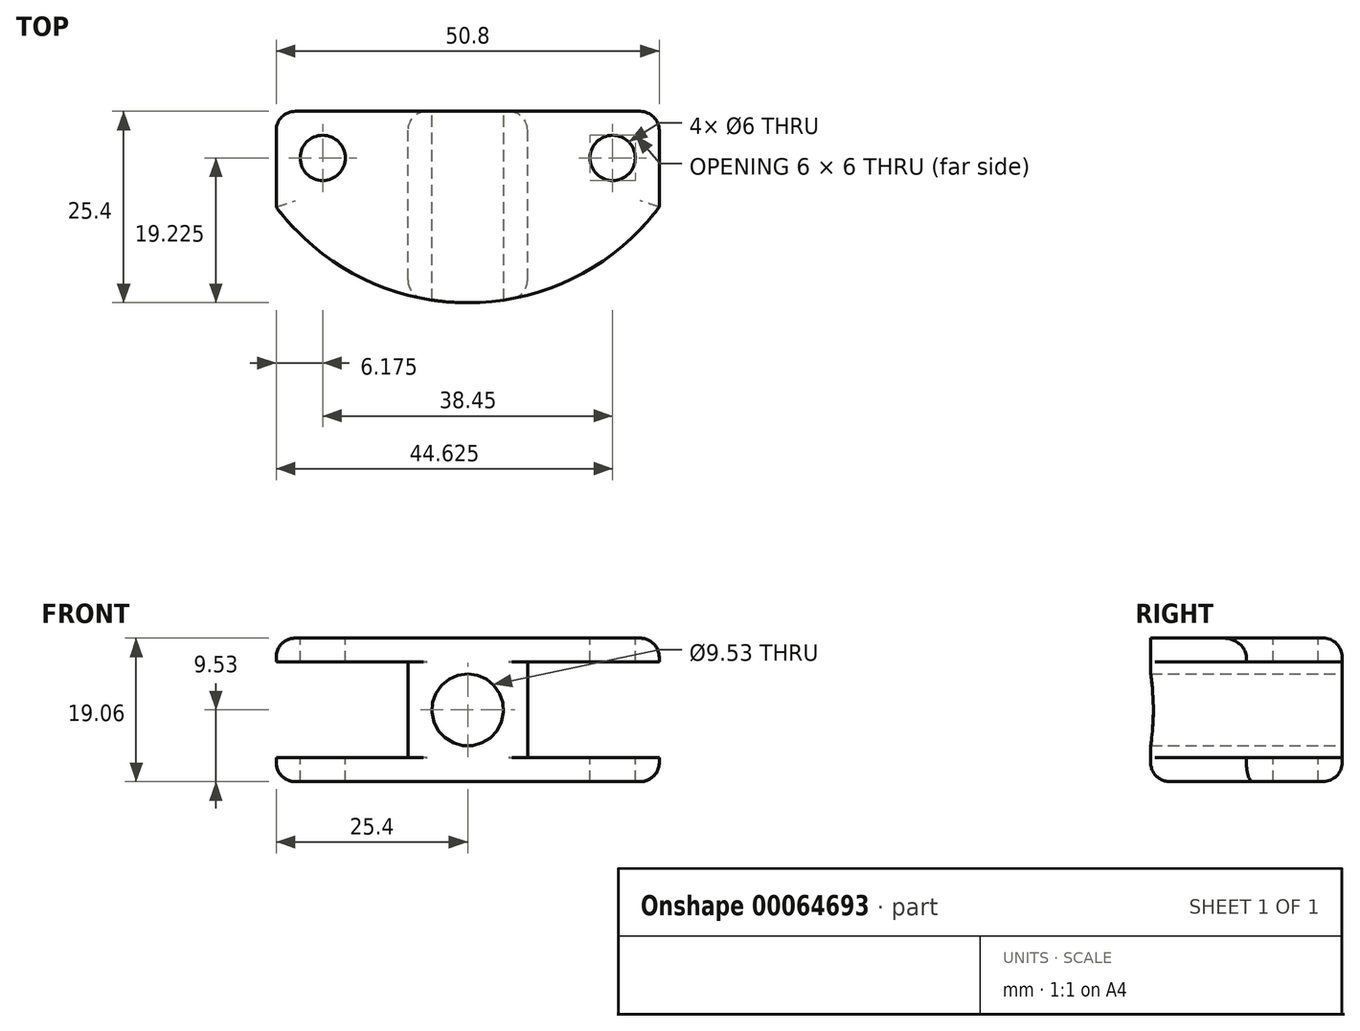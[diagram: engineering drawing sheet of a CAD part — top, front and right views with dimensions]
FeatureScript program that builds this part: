
annotation { "Feature Type Name" : "Feature", "Feature Type Description" : "" }
export const myFeature = defineFeature(function(context is Context, id is Id, definition is map)
    precondition{}
    {
        {
            var Q0;
            Q0=qCreatedBy(makeId("Front.planeOp"),FACE);
            var sketch = newSketch(context, id + "F0", { "sketchPlane" : qUnion([Q0])});
            skLineSegment(sketch, "E0", {"start": v(0, 19.05) * mm, "end": v(-38.1, 19.05) * mm});
            skLineSegment(sketch, "E1", {"start": v(-38.1, 19.05) * mm, "end": v(-38.1, 12.7) * mm});
            skLineSegment(sketch, "E2", {"start": v(0, -19.05) * mm, "end": v(-38.1, -19.05) * mm});
            skLineSegment(sketch, "E3", {"start": v(-38.1, -19.05) * mm, "end": v(-38.1, -12.7) * mm});
            skLineSegment(sketch, "E4", {"start": v(-38.1, 12.7) * mm, "end": v(-15.88, 12.7) * mm});
            skLineSegment(sketch, "E5", {"start": v(-15.88, 12.7) * mm, "end": v(-15.88, -12.7) * mm});
            skLineSegment(sketch, "E6", {"start": v(-15.88, -12.7) * mm, "end": v(-38.1, -12.7) * mm});
            skLineSegment(sketch, "E7.MirrorCS", {"start": v(0, 19.05) * mm, "end": v(38.1, 19.05) * mm});
            skLineSegment(sketch, "E8.MirrorCS", {"start": v(38.1, 19.05) * mm, "end": v(38.1, 12.7) * mm});
            skLineSegment(sketch, "E9.MirrorCS", {"start": v(38.1, 12.7) * mm, "end": v(15.88, 12.7) * mm});
            skLineSegment(sketch, "E10.MirrorCS", {"start": v(15.88, 12.7) * mm, "end": v(15.88, -12.7) * mm});
            skLineSegment(sketch, "E11.MirrorCS", {"start": v(15.88, -12.7) * mm, "end": v(38.1, -12.7) * mm});
            skLineSegment(sketch, "E12.MirrorCS", {"start": v(38.1, -19.05) * mm, "end": v(38.1, -12.7) * mm});
            skLineSegment(sketch, "E13.MirrorCS", {"start": v(0, -19.05) * mm, "end": v(38.1, -19.05) * mm});
            skSolve(sketch);
        }
        {
            var Q0;
            Q0=makeQuery(id+"F0.imprint","IMPRINT",FACE,{"disambiguationData":[TD([[makeQuery(id+"F0.imprint","IMPRINT",EDGE,{"derivedFrom":sQuery(id+"F0.wireOp",EDGE,"E0")}),1.0]])]});
            extrude(context, id + "F1", {"entities" : qUnion([Q0]), "depth" : 50.8 * mm});
        }
        {
            var Q0;
            Q0=makeQuery(id+"F1.opExtrude","SWEPT_FACE",FACE,{"disambiguationData":[OSD([sQuery(id+"F0.wireOp",EDGE,"E1")])]});
            var Q1;
            Q1=makeQuery(id+"F1.opExtrude","SWEPT_FACE",FACE,{"disambiguationData":[OSD([sQuery(id+"F0.wireOp",EDGE,"E3")])]});
            extrude(context, id + "F2", {"entities" : qUnion([Q0, Q1]), "operationType" : NewBodyOperationType.ADD, "depth" : 12.7 * mm});
        }
        {
            var Q0;
            Q0=makeQuery(id+"F1.opExtrude","SWEPT_FACE",FACE,{"disambiguationData":[OSD([sQuery(id+"F0.wireOp",EDGE,"E8.MirrorCS")])]});
            var Q1;
            Q1=makeQuery(id+"F1.opExtrude","SWEPT_FACE",FACE,{"disambiguationData":[OSD([sQuery(id+"F0.wireOp",EDGE,"E12.MirrorCS")])]});
            extrude(context, id + "F3", {"entities" : qUnion([Q0, Q1]), "operationType" : NewBodyOperationType.ADD, "depth" : 12.7 * mm});
        }
        {
            var Q0;
            {var subQ0=sQuery(id+"F0.wireOp",EDGE,"E7.MirrorCS");var subQ1=sQuery(id+"F0.wireOp",EDGE,"E0");Q0=makeQuery(id+"F3.boolean.opBoolean","MERGE",FACE,{"derivedFrom":[makeQuery(id+"F2.boolean.opBoolean","MERGE",FACE,{"derivedFrom":[makeQuery(id+"F1.opExtrude","SWEPT_FACE",FACE,{"disambiguationData":[OSD([subQ1,subQ0])]}),makeQuery(id+"F2.opExtrude","SWEPT_FACE",FACE,{"disambiguationData":[OSD([subQ1,sQuery(id+"F0.wireOp",EDGE,"E1")])]})]}),makeQuery(id+"F3.opExtrude","SWEPT_FACE",FACE,{"disambiguationData":[OSD([subQ0,sQuery(id+"F0.wireOp",EDGE,"E8.MirrorCS")])]})]});}
            var sketch = newSketch(context, id + "F4", { "sketchPlane" : qUnion([Q0])});
            skCircle(sketch, "E14", {"center": v(38.45, -12.35) * mm, "radius": 6 * mm});
            skLineSegment(sketch, "E15", {"start": v(0, 0) * mm, "end": v(0, -50.8) * mm});
            skCircle(sketch, "E16.MirrorC", {"center": v(-38.45, -12.35) * mm, "radius": 6 * mm});
            skArc(sketch, "E17", {"start": v(-50.8, -25.4) * mm, "mid": v(0, -50.8) * mm, "end": v(50.8, -25.4) * mm});
            skSolve(sketch);
        }
        {
            var Q0;
            Q0 = qSketchRegion(id + "F4", true);
            extrude(context, id + "F5", {"entities" : qUnion([Q0]), "operationType" : NewBodyOperationType.REMOVE, "oppositeDirection" : true, "depth" : 53.43 * mm});
        }
        {
            var Q0;
            {var subQ0=sQuery(id+"F4.wireOp",EDGE,"E17");var subQ3=sQuery(id+"F0.wireOp",EDGE,"E1");var subQ4=sQuery(id+"F0.wireOp",EDGE,"E0");var subQ7=makeQuery(id+"F2.opExtrude","CAP_EDGE",EDGE,{"disambiguationData":[OSD([subQ4,subQ3])],"isStart":false});var subQ8=makeQuery(id+"F4.imprint","INTERSECT",VERTEX,{"derivedFrom":[subQ7,subQ0]});Q0=makeQuery(id+"F4.imprint","IMPRINT",FACE,{"disambiguationData":[TD([[makeQuery(id+"F4.imprint","IMPRINT",EDGE,{"disambiguationData":[TD([[subQ8,-1.0]])],"derivedFrom":subQ0}),-1.0]])]});}
            var Q1;
            {var subQ0=sQuery(id+"F4.wireOp",EDGE,"E17");var subQ1=sQuery(id+"F0.wireOp",EDGE,"E8.MirrorCS");var subQ2=sQuery(id+"F0.wireOp",EDGE,"E7.MirrorCS");var subQ7=makeQuery(id+"F3.opExtrude","CAP_EDGE",EDGE,{"disambiguationData":[OSD([subQ2,subQ1])],"isStart":false});var subQ8=makeQuery(id+"F4.imprint","INTERSECT",VERTEX,{"derivedFrom":[subQ7,subQ0]});Q1=makeQuery(id+"F4.imprint","IMPRINT",FACE,{"disambiguationData":[TD([[makeQuery(id+"F4.imprint","IMPRINT",EDGE,{"disambiguationData":[TD([[subQ8,1.0]])],"derivedFrom":subQ0}),-1.0]])]});}
            extrude(context, id + "F6", {"entities" : qUnion([Q0, Q1]), "operationType" : NewBodyOperationType.REMOVE, "oppositeDirection" : true, "depth" : 44.17 * mm});
        }
        {
            var Q0;
            {var subQ0=sQuery(id+"F0.wireOp",EDGE,"E12.MirrorCS");var subQ1=sQuery(id+"F0.wireOp",EDGE,"E8.MirrorCS");var subQ2=sQuery(id+"F0.wireOp",EDGE,"E3");var subQ3=sQuery(id+"F0.wireOp",EDGE,"E1");Q0=makeQuery(id+"F3.boolean.opBoolean","MERGE",FACE,{"derivedFrom":[makeQuery(id+"F2.boolean.opBoolean","MERGE",FACE,{"derivedFrom":[makeQuery(id+"F1.opExtrude","CAP_FACE",FACE,{"disambiguationData":[OSD([sQuery(id+"F0.wireOp",EDGE,"E0"),subQ3,sQuery(id+"F0.wireOp",EDGE,"E2"),subQ2,sQuery(id+"F0.wireOp",EDGE,"E4"),sQuery(id+"F0.wireOp",EDGE,"E5"),sQuery(id+"F0.wireOp",EDGE,"E6"),sQuery(id+"F0.wireOp",EDGE,"E7.MirrorCS"),subQ1,sQuery(id+"F0.wireOp",EDGE,"E9.MirrorCS"),sQuery(id+"F0.wireOp",EDGE,"E10.MirrorCS"),sQuery(id+"F0.wireOp",EDGE,"E11.MirrorCS"),subQ0,sQuery(id+"F0.wireOp",EDGE,"E13.MirrorCS")])],"isStart":true}),makeQuery(id+"F2.opExtrude","SWEPT_FACE",FACE,{"disambiguationData":[OSD([subQ3]),TDD([makeQuery(id+"F1.opExtrude","CAP_EDGE",EDGE,{"disambiguationData":[OSD([subQ3])],"isStart":true})])]}),makeQuery(id+"F2.opExtrude","SWEPT_FACE",FACE,{"disambiguationData":[OSD([subQ2]),TDD([makeQuery(id+"F1.opExtrude","CAP_EDGE",EDGE,{"disambiguationData":[OSD([subQ2])],"isStart":true})])]})]}),makeQuery(id+"F3.opExtrude","SWEPT_FACE",FACE,{"disambiguationData":[OSD([subQ1]),TDD([makeQuery(id+"F1.opExtrude","CAP_EDGE",EDGE,{"disambiguationData":[OSD([subQ1])],"isStart":true})])]}),makeQuery(id+"F3.opExtrude","SWEPT_FACE",FACE,{"disambiguationData":[OSD([subQ0]),TDD([makeQuery(id+"F1.opExtrude","CAP_EDGE",EDGE,{"disambiguationData":[OSD([subQ0])],"isStart":true})])]})]});}
            var sketch = newSketch(context, id + "F7", { "sketchPlane" : qUnion([Q0])});
            skCircle(sketch, "E18", {"center": v(0, 0) * mm, "radius": 9.53 * mm});
            skSolve(sketch);
        }
        {
            var Q0;
            Q0=makeQuery(id+"F7.imprint","IMPRINT",FACE,{"disambiguationData":[TD([[makeQuery(id+"F7.imprint","IMPRINT",EDGE,{"derivedFrom":sQuery(id+"F7.wireOp",EDGE,"E18")}),1.0]])]});
            extrude(context, id + "F8", {"entities" : qUnion([Q0]), "operationType" : NewBodyOperationType.REMOVE, "oppositeDirection" : true, "depth" : 88.3 * mm});
        }
        {
            var Q0;
            {var subQ0=sQuery(id+"F0.wireOp",EDGE,"E1");Q0=makeQuery(id+"F2.opExtrude","CAP_EDGE",EDGE,{"disambiguationData":[OSD([subQ0]),TDD([makeQuery(id+"F1.opExtrude","CAP_EDGE",EDGE,{"disambiguationData":[OSD([subQ0])],"isStart":true})])],"isStart":false});}
            var Q1;
            {var subQ0=sQuery(id+"F0.wireOp",EDGE,"E3");Q1=makeQuery(id+"F2.opExtrude","CAP_EDGE",EDGE,{"disambiguationData":[OSD([subQ0]),TDD([makeQuery(id+"F1.opExtrude","CAP_EDGE",EDGE,{"disambiguationData":[OSD([subQ0])],"isStart":true})])],"isStart":false});}
            var Q2;
            {var subQ0=sQuery(id+"F0.wireOp",EDGE,"E8.MirrorCS");Q2=makeQuery(id+"F3.opExtrude","CAP_EDGE",EDGE,{"disambiguationData":[OSD([subQ0]),TDD([makeQuery(id+"F1.opExtrude","CAP_EDGE",EDGE,{"disambiguationData":[OSD([subQ0])],"isStart":true})])],"isStart":false});}
            var Q3;
            {var subQ0=sQuery(id+"F0.wireOp",EDGE,"E12.MirrorCS");Q3=makeQuery(id+"F3.opExtrude","CAP_EDGE",EDGE,{"disambiguationData":[OSD([subQ0]),TDD([makeQuery(id+"F1.opExtrude","CAP_EDGE",EDGE,{"disambiguationData":[OSD([subQ0])],"isStart":true})])],"isStart":false});}
            var Q4;
            {var subQ0=sQuery(id+"F0.wireOp",EDGE,"E13.MirrorCS");var subQ1=sQuery(id+"F0.wireOp",EDGE,"E12.MirrorCS");var subQ2=sQuery(id+"F0.wireOp",EDGE,"E3");var subQ3=sQuery(id+"F0.wireOp",EDGE,"E2");Q4=makeQuery(id+"F3.boolean.opBoolean","MERGE",EDGE,{"derivedFrom":[makeQuery(id+"F2.boolean.opBoolean","MERGE",EDGE,{"derivedFrom":[makeQuery(id+"F1.opExtrude","CAP_EDGE",EDGE,{"disambiguationData":[OSD([subQ3,subQ0])],"isStart":true}),makeQuery(id+"F2.opExtrude","SWEPT_EDGE",EDGE,{"disambiguationData":[OSD([subQ3,subQ2]),TDD([makeQuery(id+"F1.opExtrude","CAP_VERTEX",VERTEX,{"disambiguationData":[OSD([subQ3,subQ2])],"isStart":true})])]})]}),makeQuery(id+"F3.opExtrude","SWEPT_EDGE",EDGE,{"disambiguationData":[OSD([subQ1,subQ0]),TDD([makeQuery(id+"F1.opExtrude","CAP_VERTEX",VERTEX,{"disambiguationData":[OSD([subQ1,subQ0])],"isStart":true})])]})]});}
            var Q5;
            {var subQ0=sQuery(id+"F0.wireOp",EDGE,"E8.MirrorCS");var subQ1=sQuery(id+"F0.wireOp",EDGE,"E7.MirrorCS");var subQ2=sQuery(id+"F0.wireOp",EDGE,"E1");var subQ3=sQuery(id+"F0.wireOp",EDGE,"E0");Q5=makeQuery(id+"F3.boolean.opBoolean","MERGE",EDGE,{"derivedFrom":[makeQuery(id+"F2.boolean.opBoolean","MERGE",EDGE,{"derivedFrom":[makeQuery(id+"F1.opExtrude","CAP_EDGE",EDGE,{"disambiguationData":[OSD([subQ3,subQ1])],"isStart":true}),makeQuery(id+"F2.opExtrude","SWEPT_EDGE",EDGE,{"disambiguationData":[OSD([subQ3,subQ2]),TDD([makeQuery(id+"F1.opExtrude","CAP_VERTEX",VERTEX,{"disambiguationData":[OSD([subQ3,subQ2])],"isStart":true})])]})]}),makeQuery(id+"F3.opExtrude","SWEPT_EDGE",EDGE,{"disambiguationData":[OSD([subQ1,subQ0]),TDD([makeQuery(id+"F1.opExtrude","CAP_VERTEX",VERTEX,{"disambiguationData":[OSD([subQ1,subQ0])],"isStart":true})])]})]});}
            var Q6;
            Q6=makeQuery(id+"F2.opExtrude","CAP_EDGE",EDGE,{"disambiguationData":[OSD([sQuery(id+"F0.wireOp",EDGE,"E0"),sQuery(id+"F0.wireOp",EDGE,"E1")])],"isStart":false});
            var Q7;
            Q7=makeQuery(id+"F3.opExtrude","CAP_EDGE",EDGE,{"disambiguationData":[OSD([sQuery(id+"F0.wireOp",EDGE,"E7.MirrorCS"),sQuery(id+"F0.wireOp",EDGE,"E8.MirrorCS")])],"isStart":false});
            var Q8;
            Q8=makeQuery(id+"F3.opExtrude","CAP_EDGE",EDGE,{"disambiguationData":[OSD([sQuery(id+"F0.wireOp",EDGE,"E12.MirrorCS"),sQuery(id+"F0.wireOp",EDGE,"E13.MirrorCS")])],"isStart":false});
            var Q9;
            Q9=makeQuery(id+"F2.opExtrude","CAP_EDGE",EDGE,{"disambiguationData":[OSD([sQuery(id+"F0.wireOp",EDGE,"E2"),sQuery(id+"F0.wireOp",EDGE,"E3")])],"isStart":false});
            var Q10;
            {var subQ0=sQuery(id+"F4.wireOp",EDGE,"E17");var subQ1=sQuery(id+"F0.wireOp",EDGE,"E8.MirrorCS");var subQ2=sQuery(id+"F0.wireOp",EDGE,"E7.MirrorCS");var subQ3=sQuery(id+"F0.wireOp",EDGE,"E1");var subQ4=sQuery(id+"F0.wireOp",EDGE,"E0");Q10=makeQuery(id+"F6.boolean.opBoolean","TWEAK_EDGE",EDGE,{"derivedFrom":[makeQuery(id+"F6.opExtrude","CAP_EDGE",EDGE,{"disambiguationData":[OSD([subQ0]),TDD([makeQuery(id+"F4.imprint","IMPRINT",EDGE,{"disambiguationData":[TD([[makeQuery(id+"F4.imprint","INTERSECT",VERTEX,{"derivedFrom":[makeQuery(id+"F2.opExtrude","CAP_EDGE",EDGE,{"disambiguationData":[OSD([subQ4,subQ3])],"isStart":false}),subQ0]}),-1.0]])],"derivedFrom":subQ0})])],"isStart":true}),makeQuery(id+"F6.opExtrude","CAP_EDGE",EDGE,{"disambiguationData":[OSD([subQ0]),TDD([makeQuery(id+"F4.imprint","IMPRINT",EDGE,{"disambiguationData":[TD([[makeQuery(id+"F4.imprint","INTERSECT",VERTEX,{"derivedFrom":[makeQuery(id+"F3.opExtrude","CAP_EDGE",EDGE,{"disambiguationData":[OSD([subQ2,subQ1])],"isStart":false}),subQ0]}),1.0]])],"derivedFrom":subQ0})])],"isStart":true})]});}
            var Q11;
            {var subQ0=sQuery(id+"F4.wireOp",EDGE,"E17");var subQ1=sQuery(id+"F0.wireOp",EDGE,"E8.MirrorCS");var subQ2=sQuery(id+"F0.wireOp",EDGE,"E7.MirrorCS");var subQ3=sQuery(id+"F0.wireOp",EDGE,"E1");var subQ4=sQuery(id+"F0.wireOp",EDGE,"E0");var subQ6=sQuery(id+"F0.wireOp",EDGE,"E13.MirrorCS");var subQ7=sQuery(id+"F0.wireOp",EDGE,"E2");Q11=makeQuery(id+"F6.boolean.opBoolean","INTERSECT",EDGE,{"derivedFrom":[makeQuery(id+"F3.boolean.opBoolean","MERGE",FACE,{"derivedFrom":[makeQuery(id+"F2.boolean.opBoolean","MERGE",FACE,{"derivedFrom":[makeQuery(id+"F1.opExtrude","SWEPT_FACE",FACE,{"disambiguationData":[OSD([subQ7,subQ6])]}),makeQuery(id+"F2.opExtrude","SWEPT_FACE",FACE,{"disambiguationData":[OSD([subQ7,sQuery(id+"F0.wireOp",EDGE,"E3")])]})]}),makeQuery(id+"F3.opExtrude","SWEPT_FACE",FACE,{"disambiguationData":[OSD([sQuery(id+"F0.wireOp",EDGE,"E12.MirrorCS"),subQ6])]})]}),makeQuery(id+"F6.opExtrude","SWEPT_FACE",FACE,{"disambiguationData":[OSD([subQ0]),TDD([makeQuery(id+"F4.imprint","IMPRINT",EDGE,{"disambiguationData":[TD([[makeQuery(id+"F4.imprint","INTERSECT",VERTEX,{"derivedFrom":[makeQuery(id+"F2.opExtrude","CAP_EDGE",EDGE,{"disambiguationData":[OSD([subQ4,subQ3])],"isStart":false}),subQ0]}),-1.0]])],"derivedFrom":subQ0})])]}),makeQuery(id+"F6.opExtrude","SWEPT_FACE",FACE,{"disambiguationData":[OSD([subQ0]),TDD([makeQuery(id+"F4.imprint","IMPRINT",EDGE,{"disambiguationData":[TD([[makeQuery(id+"F4.imprint","INTERSECT",VERTEX,{"derivedFrom":[makeQuery(id+"F3.opExtrude","CAP_EDGE",EDGE,{"disambiguationData":[OSD([subQ2,subQ1])],"isStart":false}),subQ0]}),1.0]])],"derivedFrom":subQ0})])]})]});}
            var Q12;
            {var subQ0=sQuery(id+"F4.wireOp",EDGE,"E17");var subQ3=sQuery(id+"F0.wireOp",EDGE,"E1");var subQ4=sQuery(id+"F0.wireOp",EDGE,"E0");Q12=makeQuery(id+"F6.boolean.opBoolean","INTERSECT",EDGE,{"derivedFrom":[makeQuery(id+"F1.opExtrude","SWEPT_FACE",FACE,{"disambiguationData":[OSD([sQuery(id+"F0.wireOp",EDGE,"E5")])]}),makeQuery(id+"F6.opExtrude","SWEPT_FACE",FACE,{"disambiguationData":[OSD([subQ0]),TDD([makeQuery(id+"F4.imprint","IMPRINT",EDGE,{"disambiguationData":[TD([[makeQuery(id+"F4.imprint","INTERSECT",VERTEX,{"derivedFrom":[makeQuery(id+"F2.opExtrude","CAP_EDGE",EDGE,{"disambiguationData":[OSD([subQ4,subQ3])],"isStart":false}),subQ0]}),-1.0]])],"derivedFrom":subQ0})])]})]});}
            var Q13;
            {var subQ0=sQuery(id+"F4.wireOp",EDGE,"E17");var subQ1=sQuery(id+"F0.wireOp",EDGE,"E8.MirrorCS");var subQ2=sQuery(id+"F0.wireOp",EDGE,"E7.MirrorCS");var subQ3=sQuery(id+"F0.wireOp",EDGE,"E1");var subQ4=sQuery(id+"F0.wireOp",EDGE,"E0");Q13=makeQuery(id+"F6.boolean.opBoolean","INTERSECT",EDGE,{"derivedFrom":[makeQuery(id+"F1.opExtrude","SWEPT_FACE",FACE,{"disambiguationData":[OSD([sQuery(id+"F0.wireOp",EDGE,"E10.MirrorCS")])]}),makeQuery(id+"F6.opExtrude","SWEPT_FACE",FACE,{"disambiguationData":[OSD([subQ0]),TDD([makeQuery(id+"F4.imprint","IMPRINT",EDGE,{"disambiguationData":[TD([[makeQuery(id+"F4.imprint","INTERSECT",VERTEX,{"derivedFrom":[makeQuery(id+"F2.opExtrude","CAP_EDGE",EDGE,{"disambiguationData":[OSD([subQ4,subQ3])],"isStart":false}),subQ0]}),-1.0]])],"derivedFrom":subQ0})])]}),makeQuery(id+"F6.opExtrude","SWEPT_FACE",FACE,{"disambiguationData":[OSD([subQ0]),TDD([makeQuery(id+"F4.imprint","IMPRINT",EDGE,{"disambiguationData":[TD([[makeQuery(id+"F4.imprint","INTERSECT",VERTEX,{"derivedFrom":[makeQuery(id+"F3.opExtrude","CAP_EDGE",EDGE,{"disambiguationData":[OSD([subQ2,subQ1])],"isStart":false}),subQ0]}),1.0]])],"derivedFrom":subQ0})])]})]});}
            var Q14;
            Q14=makeQuery(id+"F1.opExtrude","CAP_EDGE",EDGE,{"disambiguationData":[OSD([sQuery(id+"F0.wireOp",EDGE,"E5")])],"isStart":true});
            var Q15;
            Q15=makeQuery(id+"F1.opExtrude","CAP_EDGE",EDGE,{"disambiguationData":[OSD([sQuery(id+"F0.wireOp",EDGE,"E10.MirrorCS")])],"isStart":true});
            fillet(context, id + "F9", {"entities" : qUnion([Q0, Q1, Q2, Q3, Q4, Q5, Q6, Q7, Q8, Q9, Q10, Q11, Q12, Q13, Q14, Q15]), "radius" : 5.08 * mm, "tangentPropagation" : true, "allowEdgeOverflow" : false});
        }
        {
            var Q0;
            Q0=makeQuery(id+"F1.opExtrude","SWEPT_BODY",BODY,{"disambiguationData":[OSD([sQuery(id+"F0.wireOp",EDGE,"E0"),sQuery(id+"F0.wireOp",EDGE,"E1"),sQuery(id+"F0.wireOp",EDGE,"E2"),sQuery(id+"F0.wireOp",EDGE,"E3"),sQuery(id+"F0.wireOp",EDGE,"E4"),sQuery(id+"F0.wireOp",EDGE,"E5"),sQuery(id+"F0.wireOp",EDGE,"E6"),sQuery(id+"F0.wireOp",EDGE,"E7.MirrorCS"),sQuery(id+"F0.wireOp",EDGE,"E8.MirrorCS"),sQuery(id+"F0.wireOp",EDGE,"E9.MirrorCS"),sQuery(id+"F0.wireOp",EDGE,"E10.MirrorCS"),sQuery(id+"F0.wireOp",EDGE,"E11.MirrorCS"),sQuery(id+"F0.wireOp",EDGE,"E12.MirrorCS"),sQuery(id+"F0.wireOp",EDGE,"E13.MirrorCS")])]});
            var Q1;
            Q1=qCreatedBy(makeId("Origin.pointOp"),VERTEX);
            transform(context, id + "F10", {"entities" : qUnion([Q0]), "transformType" : TransformType.SCALE_UNIFORMLY, "scale" : .5, "scalePoint" : qUnion([Q1]), "makeCopy" : false});
        }
    });
